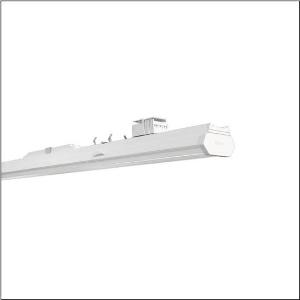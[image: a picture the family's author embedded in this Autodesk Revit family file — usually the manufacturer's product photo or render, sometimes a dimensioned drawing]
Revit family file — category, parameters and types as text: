
# Revit family: licross_11_protected_mo_51tp127n485g
name_source: partatom
category: Lighting Fixtures
units: mm (PartAtom-declared; Revit-internal decimal feet)

## family parameters
Cut with Voids When Loaded = No
Host = Face
Light Source = No
Part Type = Normal
Room Calculation Point = No
Round Connector Dimension = Use Diameter
Shared = No

## types (1)
- Licross 11 Protected MO (1 x LED, 8720 lm, 48.6 W, 4000K)
    Apparent Load = 49 VA
    CIE Flux Codes = 73 92 98 99 100
    Color Rendering = 80
    Color Temperature = 4000K
    Default Elevation = 1800 mm
    Description = Licross 11 Protected MO, luminaire insert, of sheet steel, galvanised, coil coated, white, length: 1.500mm, width: 90mm, height: 101mm, LED rated luminous flux: 8.720lm, light colour: 840, SDCM (Standard Deviation of Colour Matching)MacAdam ≤ 2 SDCM (initial), control gear: ON/OFF, with plug, 3-pole, with phase selection, mains connection: 220..240V, AC, 50/60Hz, rated input power: 49W, internal wiring halogen-free, primary light control with lens, of plastic, primary optical cover: cover, of PMMA, light emission: direct distribution, primary light characteristic: symmetric, protection rating (complete): IP64, insulation class (complete): insulation class I (protective earthing), certification: CE, ENEC, VDE, UKCA, protection symbol: D if used in an environment with conductive dust loads with corresponding accessories, impact resistance: IK06, permissible ambient temperature for indoor applications: -25..+35°C, corresponds to IFS (International Featured Standards) requirements for safety and quality in the food industry, reducing of maximum allowable ambient temperature of 5°C with ceiling mounting, LABS conformity tested according to VDMA 24364:2018-05, The light source and the operating device comply with the requirements of the Ecodesign Regulation (EU) 2019/2020 and are replaceable in accordance with this regulation, packaging unit: 1 piece
    Height = 92 mm
    Lamp = 1 x LED
    Lamp Light Flux = 8720 lm
    Lamp Power = 48.6 W
    Lamp count = 1
    Length = 1500 mm
    Luminous efficacy = 179 lm/W
    Manufacturer = Siteco
    ModVariant = No
    Model = 51TP127N485G
    Mounting Place = Ceiling
    Mounting Type = Pendant
    Number of Poles = 1
    OnlyDefault = Yes
    Power Factor = 1
    Product Name = Licross 11 Protected MO
    Product group = luminaire insert | ceiling pendant
    ProductGroupID = 901
    Protection Class = Protection class I
    Protection Degree = IP 64
    RLX_Detail_Level = 1
    RLX_Emergency_Light_Flux = 0 lm
    RLX_Emergency_Type = 0
    RLX_Emergency_Type_DB = No
    RlxData = <blob elided: 21025 chars, md5=bf413c55>
    Socket = socket
    Standby Power = 0 W
    System Light Flux = 8720 lm
    System Power = 49 W
    Type Comments = Product without accessories
    Type Image = l_1256148.jpg
    URL = http://relux.com
    VarID = ---
    Voltage = 0 V
    Weight = 0.00 kg
    Width = 88 mm

## geometry (parser evidence)
native form markers: Blend x4, Sweep x12
no freeform markers — native parametric forms only
